# Revit family: Shower-Shower_Column_Kit-KOHLER-SINGULIER-K-72671T_1
name_source: partatom
category: Plumbing Fixtures
revit_build: Autodesk Revit 2017 (Build: 20160225_1515(x64)
units: mm (PartAtom-declared; Revit-internal decimal feet)

## family parameters
Cut with Voids When Loaded = No
Host = Face
OmniClass Number = 23.31.17.00
OmniClass Title = Showers
Part Type = Normal
Room Calculation Point = No
Round Connector Dimension = Use Diameter
Shared = No

## types (4) — shared parameters
ADA Compliant = No
Assembly Code = D2010700
CW Connection = Yes
Cold Water Inlet = Cold Water Inlet
Date Modified = 09/21/2020
Default Elevation = 42"
Drain Included = No
Flow Rate = 0 GPM
HW Connection = Yes
Height = 48 1/8"
Hot Water Inlet = Hot Water Inlet
Length = 23 7/16"
Manufacturer = KOHLER Co.
Master Format 2014 = 22 42 23
Master Format 2014 Name = Residential Showers
Material = Premium Metal Construction
Pressure = 0.00 psi
Product Name = SINGULIER
Spout Reach = 7 5/16"
URL = http://www.kohler.com.cn
Vent Connection = No
Waste Connection = No
Waste Water Outlet = Waste Water Outlet
WaterSense Certified = No
Width = 5 15/16"

## per-type parameters (varying)
| type | Description | Finish | Model | Product Documentation Link | Product Page URL | Type |
| CP-Polished Chrome | Thermostatic three-outlet right-angle shower column | Kohler-Metal-CP-Polished_Chrome | K-72671T-C9-CP | https://files.kohler.com.cn | https://www.kohler.com.cn | 1 |
| AF-Flange Gold | Thermostatic three-outlet right-angle shower column | Kohler-Metal-AF-Flange_Gold | K-72671T-C9-AF | https://files.kohler.com.cn | https://www.kohler.com.cn | 2 |
| BN-Roman Silver | Thermostatic three-outlet right-angle shower column | Kohler-Metal-BN-Roman_Silver | K-72671T-C9-BN | https://files.kohler.com.cn | https://www.kohler.com.cn | 3 |
| C9E2,CP- Polished Chrome | Thermostatic wall mount straight shower column | Kohler-Metal-CP-Polished_Chrome | K-72671T-C9E2-CP |  |  | 4 |

## geometry (parser evidence)
native form markers: Sweep x4
no freeform markers — native parametric forms only
